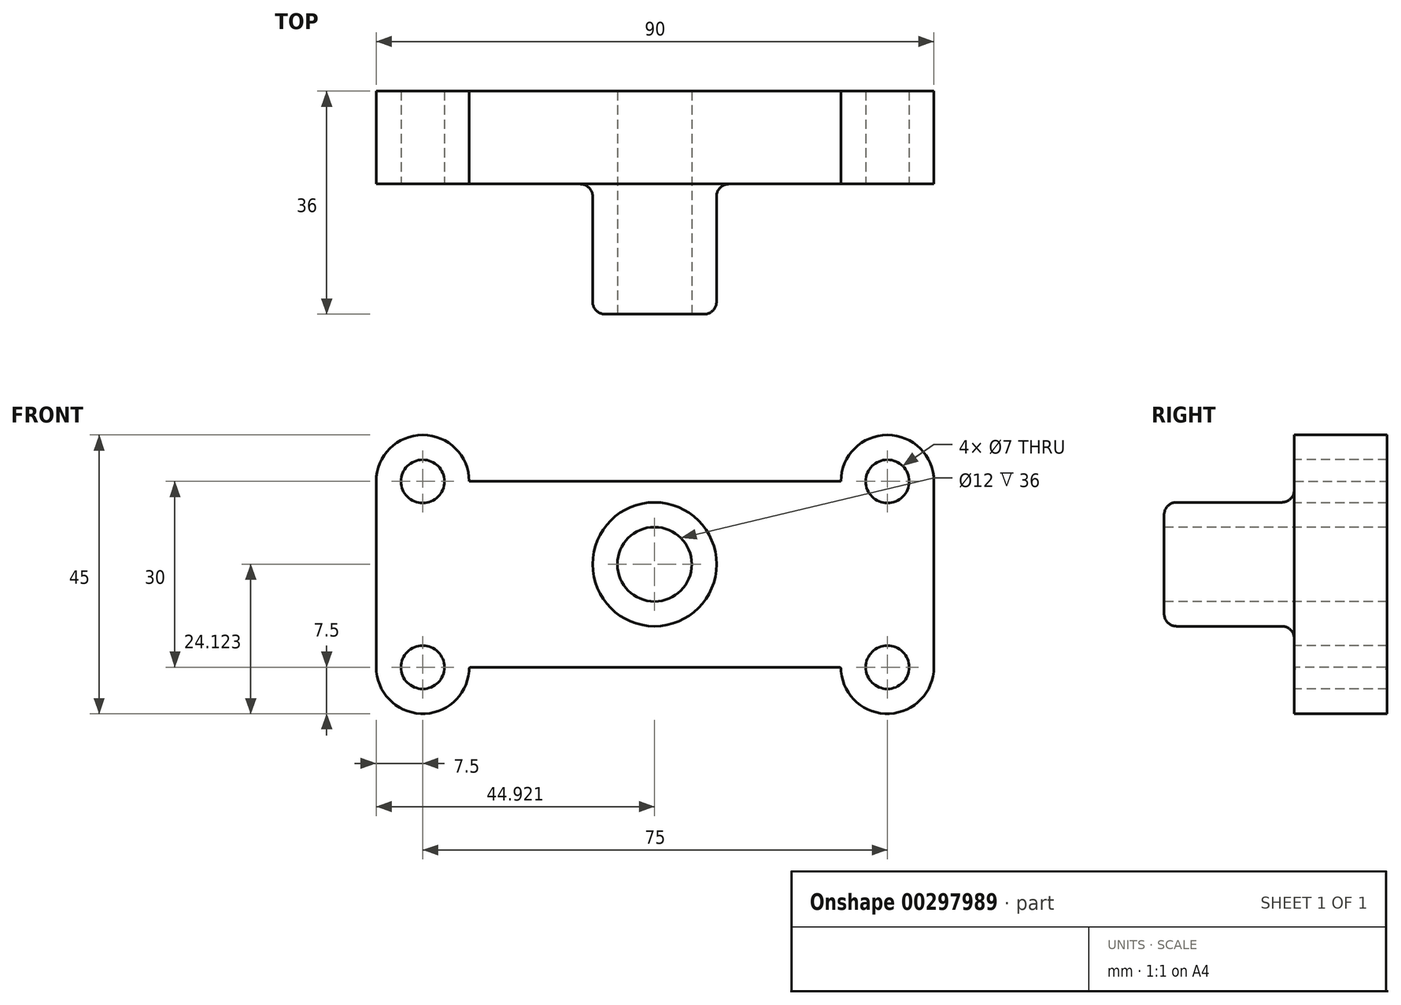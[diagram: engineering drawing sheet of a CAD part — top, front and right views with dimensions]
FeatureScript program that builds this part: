
annotation { "Feature Type Name" : "Feature", "Feature Type Description" : "" }
export const myFeature = defineFeature(function(context is Context, id is Id, definition is map)
    precondition{}
    {
        {
            var Q0;
            Q0=qCreatedBy(makeId("Front.planeOp"),FACE);
            var sketch = newSketch(context, id + "F0", { "sketchPlane" : qUnion([Q0])});
            skLineSegment(sketch, "E0.bottom", {"start": v(0, 0) * mm, "end": v(60, 0) * mm});
            skLineSegment(sketch, "E0.top", {"start": v(0, 30) * mm, "end": v(60, 30) * mm});
            skLineSegment(sketch, "E1.left", {"start": v(-15, 30) * mm, "end": v(-15, 0) * mm});
            skArc(sketch, "E2", {"start": v(0, 30) * mm, "mid": v(-7.5, 37.5) * mm, "end": v(-15, 30) * mm});
            skArc(sketch, "E3", {"start": v(-15, 0) * mm, "mid": v(-7.5, -7.5) * mm, "end": v(0, 0) * mm});
            skArc(sketch, "E4.MirrorCS", {"start": v(60, 30) * mm, "mid": v(67.5, 37.5) * mm, "end": v(75, 30) * mm});
            skLineSegment(sketch, "E5.MirrorCS", {"start": v(75, 30) * mm, "end": v(75, 0) * mm});
            skArc(sketch, "E6.MirrorCS", {"start": v(75, 0) * mm, "mid": v(67.5, -7.5) * mm, "end": v(60, 0) * mm});
            skSolve(sketch);
        }
        {
            var Q0;
            Q0=makeQuery(id+"F0.imprint","IMPRINT",FACE,{"disambiguationData":[TD([[makeQuery(id+"F0.imprint","IMPRINT",EDGE,{"derivedFrom":sQuery(id+"F0.wireOp",EDGE,"E0.bottom")}),1.0]])]});
            extrude(context, id + "F1", {"entities" : qUnion([Q0]), "depth" : 15 * mm});
        }
        {
            var Q0;
            Q0=qCreatedBy(makeId("Front.planeOp"),FACE);
            cPlane(context, id + "F2", {"entities" : qUnion([Q0]), "cplaneType" : CPlaneType.OFFSET, "offset" : 36 * mm, "width" : 150 * mm, "height" : 150 * mm});
        }
        {
            var Q0;
            Q0=qCreatedBy(id+"F2.planeOp",FACE);
            var sketch = newSketch(context, id + "F3", { "sketchPlane" : qUnion([Q0])});
            skCircle(sketch, "E7", {"center": v(29.92, 16.62) * mm, "radius": 10 * mm});
            skSolve(sketch);
        }
        {
            var Q0;
            Q0 = qSketchRegion(id + "F3", true);
            extrude(context, id + "F4", {"entities" : qUnion([Q0]), "operationType" : NewBodyOperationType.ADD, "endBound" : BoundingType.UP_TO_NEXT, "oppositeDirection" : true, "depth" : 25 * mm});
        }
        {
            var Q0;
            Q0=makeQuery(id+"F4.opExtrude","CAP_FACE",FACE,{"disambiguationData":[OSD([sQuery(id+"F3.wireOp",EDGE,"E7")])],"isStart":true});
            var sketch = newSketch(context, id + "F5", { "sketchPlane" : qUnion([Q0])});
            skCircle(sketch, "E8", {"center": v(29.92, 16.62) * mm, "radius": 6 * mm});
            skSolve(sketch);
        }
        {
            var Q0;
            Q0 = qSketchRegion(id + "F5", true);
            extrude(context, id + "F6", {"entities" : qUnion([Q0]), "operationType" : NewBodyOperationType.REMOVE, "endBound" : BoundingType.UP_TO_NEXT, "oppositeDirection" : true, "depth" : 25 * mm});
        }
        {
            var Q0;
            Q0=makeQuery(id+"F1.opExtrude","CAP_FACE",FACE,{"disambiguationData":[OSD([sQuery(id+"F0.wireOp",EDGE,"E0.bottom"),sQuery(id+"F0.wireOp",EDGE,"E0.top"),sQuery(id+"F0.wireOp",EDGE,"E1.left"),sQuery(id+"F0.wireOp",EDGE,"E2"),sQuery(id+"F0.wireOp",EDGE,"E3"),sQuery(id+"F0.wireOp",EDGE,"E4.MirrorCS"),sQuery(id+"F0.wireOp",EDGE,"E5.MirrorCS"),sQuery(id+"F0.wireOp",EDGE,"E6.MirrorCS")])],"isStart":false});
            var sketch = newSketch(context, id + "F7", { "sketchPlane" : qUnion([Q0])});
            skCircle(sketch, "E9", {"center": v(-7.5, 30) * mm, "radius": 3.5 * mm});
            skCircle(sketch, "E10", {"center": v(-7.5, 0) * mm, "radius": 3.5 * mm});
            skCircle(sketch, "E11", {"center": v(67.5, 30) * mm, "radius": 3.5 * mm});
            skCircle(sketch, "E12", {"center": v(67.5, 0) * mm, "radius": 3.5 * mm});
            skSolve(sketch);
        }
        {
            var Q0;
            Q0 = qSketchRegion(id + "F7", true);
            extrude(context, id + "F8", {"entities" : qUnion([Q0]), "operationType" : NewBodyOperationType.REMOVE, "endBound" : BoundingType.THROUGH_ALL, "oppositeDirection" : true, "depth" : 25 * mm});
        }
        {
            var Q0;
            Q0=makeQuery(id+"F4.opExtrude","SWEPT_FACE",FACE,{"disambiguationData":[OSD([sQuery(id+"F3.wireOp",EDGE,"E7")])]});
            fillet(context, id + "F9", {"entities" : qUnion([Q0]), "radius" : 2 * mm, "tangentPropagation" : true, "allowEdgeOverflow" : false});
        }
        {
            var Q0;
            Q0=makeQuery(id+"F1.opExtrude","SWEPT_FACE",FACE,{"disambiguationData":[OSD([sQuery(id+"F0.wireOp",EDGE,"E0.bottom")])]});
            fillet(context, id + "F10", {"entities" : qUnion([Q0]), "radius" : 0.25 * mm, "tangentPropagation" : true, "allowEdgeOverflow" : false});
        }
    });
